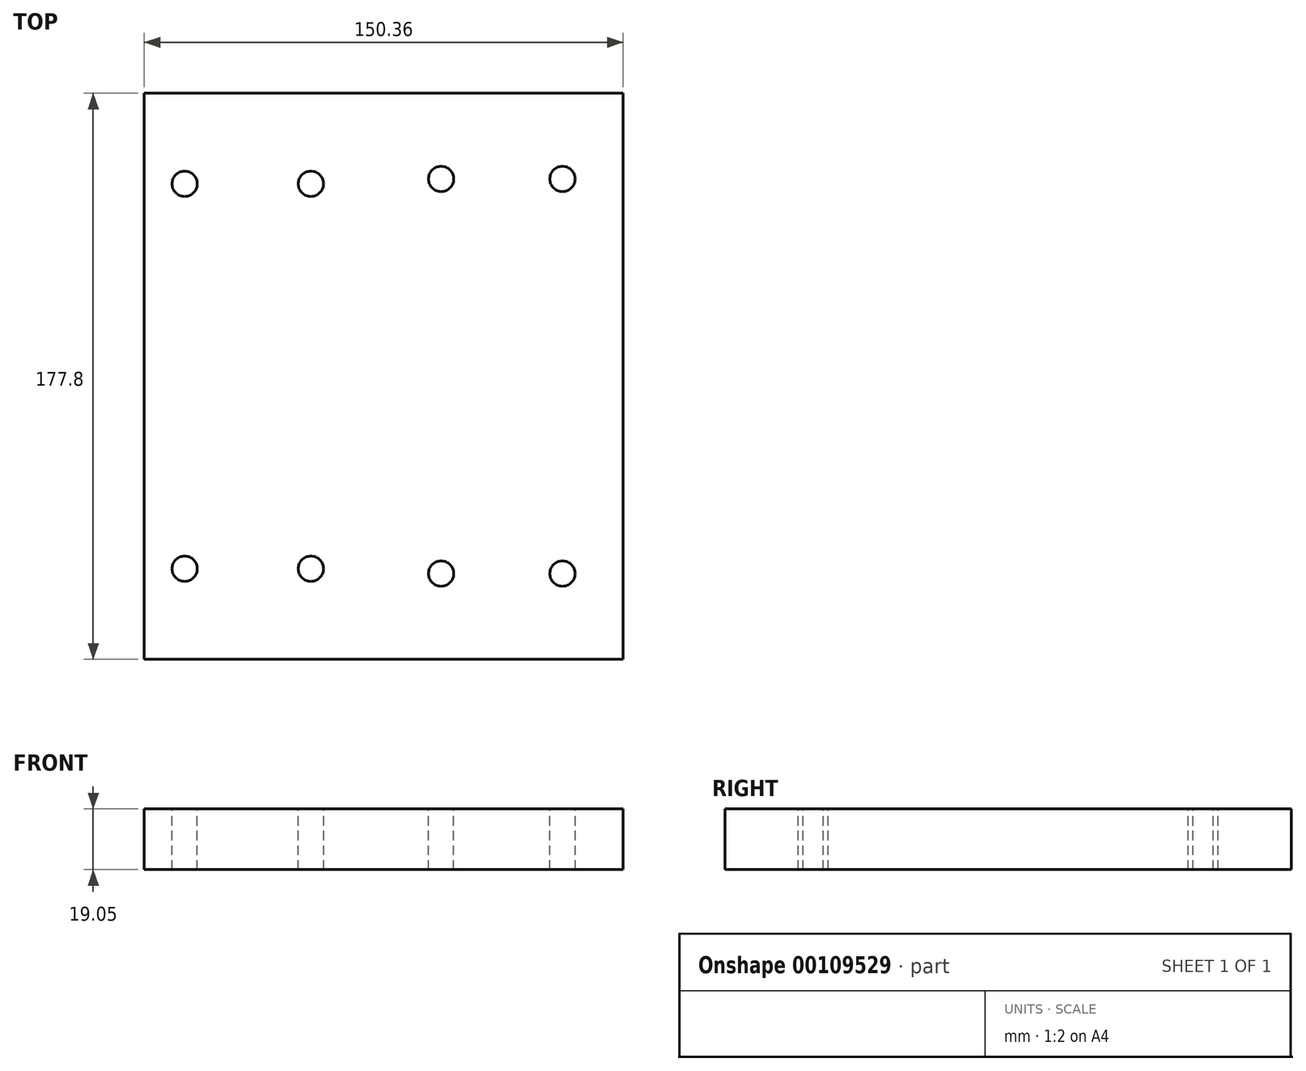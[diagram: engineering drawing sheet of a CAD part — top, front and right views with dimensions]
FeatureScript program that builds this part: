
annotation { "Feature Type Name" : "Feature", "Feature Type Description" : "" }
export const myFeature = defineFeature(function(context is Context, id is Id, definition is map)
    precondition{}
    {
        {
            var Q0;
            Q0=qCreatedBy(makeId("Top.planeOp"),FACE);
            var sketch = newSketch(context, id + "F0", { "sketchPlane" : qUnion([Q0])});
            skLineSegment(sketch, "E0.bottom", {"start": v(-75.18, 88.9) * mm, "end": v(75.18, 88.9) * mm});
            skLineSegment(sketch, "E0.top", {"start": v(-75.18, -88.9) * mm, "end": v(75.18, -88.9) * mm});
            skLineSegment(sketch, "E0.left", {"start": v(-75.18, 88.9) * mm, "end": v(-75.18, -88.9) * mm});
            skLineSegment(sketch, "E0.right", {"start": v(75.18, 88.9) * mm, "end": v(75.18, -88.9) * mm});
            skPoint(sketch, "E0.middle", {"position": v(0, 0) * mm});
            skSolve(sketch);
        }
        {
            var Q0;
            Q0=qSketchRegion(id+"F0",true);
            extrude(context, id + "F1", {"entities" : qUnion([Q0]), "depth" : 19.05 * mm, "offsetDistance" : 25.4 * mm});
        }
        {
            var Q0;
            Q0=makeQuery(id+"F1.opExtrude","CAP_FACE",FACE,{"disambiguationData":[OSD([sQuery(id+"F0.wireOp",EDGE,"E0.bottom"),sQuery(id+"F0.wireOp",EDGE,"E0.top"),sQuery(id+"F0.wireOp",EDGE,"E0.left"),sQuery(id+"F0.wireOp",EDGE,"E0.right")])],"isStart":false});
            var sketch = newSketch(context, id + "F2", { "sketchPlane" : qUnion([Q0])});
            skLineSegment(sketch, "E1", {"start": v(75.18, 0) * mm, "end": v(-75.18, 0) * mm, "construction": true});
            skLineSegment(sketch, "E2.0", {"start": v(56.13, 88.9) * mm, "end": v(56.13, -88.9) * mm, "construction": true});
            skLineSegment(sketch, "E3.0", {"start": v(18.03, 88.9) * mm, "end": v(18.03, -88.9) * mm, "construction": true});
            skLineSegment(sketch, "E4.0", {"start": v(75.18, 61.98) * mm, "end": v(18.03, 61.98) * mm, "construction": true});
            skLineSegment(sketch, "E5.MirrorCS", {"start": v(75.18, -61.98) * mm, "end": v(18.03, -61.98) * mm, "construction": true});
            skPoint(sketch, "E6.orphan", {"position": v(-75.18, 61.98) * mm});
            skPoint(sketch, "E7.orphan", {"position": v(-75.18, -61.98) * mm});
            skPoint(sketch, "E8", {"position": v(18.03, 61.98) * mm});
            skPoint(sketch, "E9", {"position": v(56.13, 61.98) * mm});
            skPoint(sketch, "E10", {"position": v(56.13, -61.98) * mm});
            skPoint(sketch, "E11", {"position": v(18.03, -61.98) * mm});
            skLineSegment(sketch, "E12.0", {"start": v(-62.48, 88.9) * mm, "end": v(-62.48, -88.9) * mm, "construction": true});
            skLineSegment(sketch, "E13.0", {"start": v(-22.86, 88.9) * mm, "end": v(-22.86, -88.9) * mm, "construction": true});
            skLineSegment(sketch, "E14.0", {"start": v(75.18, 60.45) * mm, "end": v(-75.18, 60.45) * mm, "construction": true});
            skPoint(sketch, "E15", {"position": v(-62.48, 60.45) * mm});
            skPoint(sketch, "E16", {"position": v(-22.86, 60.45) * mm});
            skPoint(sketch, "E17.MirrorP", {"position": v(-62.48, -60.45) * mm});
            skPoint(sketch, "E18.MirrorP", {"position": v(-22.86, -60.45) * mm});
            skSolve(sketch);
        }
        {
            var Q0;
            Q0=sQuery(id+"F2.wireOp",VERTEX,"E8");
            var Q1;
            Q1=sQuery(id+"F2.wireOp",VERTEX,"E9");
            var Q2;
            Q2=sQuery(id+"F2.wireOp",VERTEX,"E11");
            var Q3;
            Q3=sQuery(id+"F2.wireOp",VERTEX,"E10");
            var Q4;
            Q4=sQuery(id+"F2.wireOp",VERTEX,"E15");
            var Q5;
            Q5=sQuery(id+"F2.wireOp",VERTEX,"E16");
            var Q6;
            Q6=sQuery(id+"F2.wireOp",VERTEX,"E17.MirrorP");
            var Q7;
            Q7=sQuery(id+"F2.wireOp",VERTEX,"E18.MirrorP");
            var Q8;
            Q8=makeQuery(id+"F1.opExtrude","SWEPT_BODY",BODY,{"disambiguationData":[OSD([sQuery(id+"F0.wireOp",EDGE,"E0.bottom"),sQuery(id+"F0.wireOp",EDGE,"E0.top"),sQuery(id+"F0.wireOp",EDGE,"E0.left"),sQuery(id+"F0.wireOp",EDGE,"E0.right")])]});
            hole(context, id + "F3", {"style" : HoleStyle.SIMPLE, "endStyle" : HoleEndStyle.THROUGH, "standardTappedOrClearance" : lookupTablePath({ "standard" : "ANSI", "engagement" : "75%", "pitch" : "16 tpi", "size" : "3/8", "type" : "Tapped" }), "standardBlindInLast" : lookupTablePath({ "standard" : "ANSI", "engagement" : "75%", "pitch" : "16 tpi", "size" : "3/8", "type" : "Tapped" }), "holeDiameter" : 7.94 * mm, "majorDiameter" : 9.52 * mm, "showTappedDepth" : true, "isTappedThrough" : true, "tappedDepth" : 25.4 * mm, "tapClearance" : 3, "locations" : qUnion([Q0, Q1, Q2, Q3, Q4, Q5, Q6, Q7]), "scope" : qUnion([Q8])});
        }
    });
